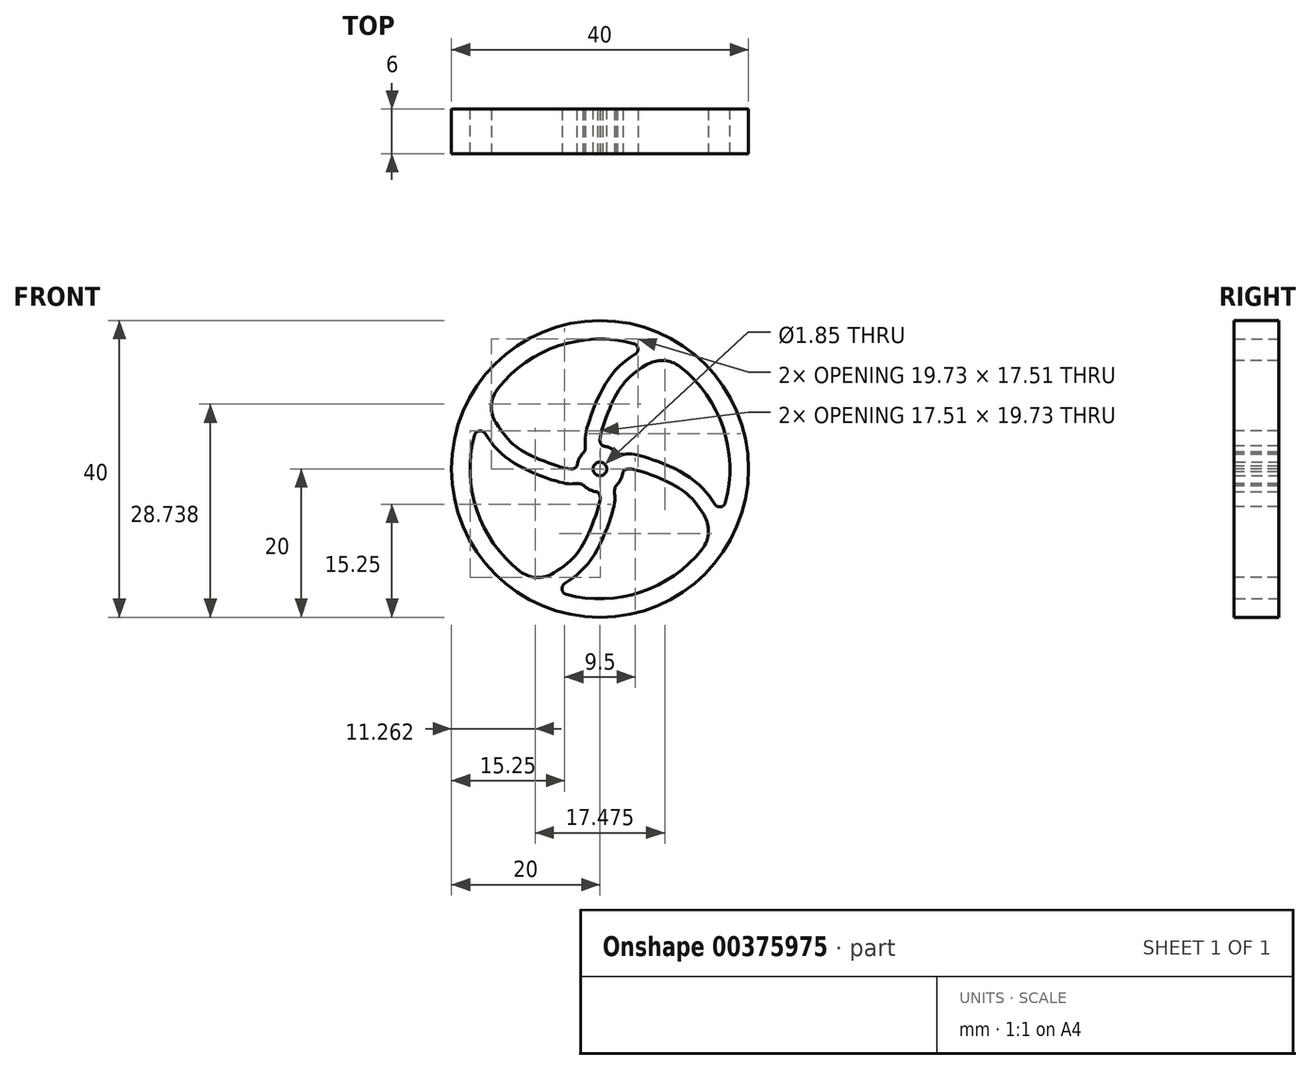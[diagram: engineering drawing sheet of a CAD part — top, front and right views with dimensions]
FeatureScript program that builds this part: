
annotation { "Feature Type Name" : "Feature", "Feature Type Description" : "" }
export const myFeature = defineFeature(function(context is Context, id is Id, definition is map)
    precondition{}
    {
        {
            var Q0;
            Q0=qCreatedBy(makeId("Front.planeOp"),FACE);
            var sketch = newSketch(context, id + "F0", { "sketchPlane" : qUnion([Q0])});
            skCircle(sketch, "E0", {"center": v(0, 0) * mm, "radius": 20 * mm});
            skCircle(sketch, "E1", {"center": v(0, 0) * mm, "radius": 0.93 * mm});
            skCircle(sketch, "E2", {"center": v(0, 0) * mm, "radius": 3.12 * mm});
            skCircle(sketch, "E3", {"center": v(0, 0) * mm, "radius": 17.5 * mm});
            skSolve(sketch);
        }
        {
            var Q0;
            Q0=qSketchRegion(id+"F0",true);
            var Q1;
            Q1=makeQuery(id+"F0.imprint","IMPRINT",FACE,{"disambiguationData":[TD([[makeQuery(id+"F0.imprint","IMPRINT",EDGE,{"derivedFrom":sQuery(id+"F0.wireOp",EDGE,"E1")}),-1.0]])]});
            extrude(context, id + "F1", {"entities" : qUnion([Q0, Q1]), "depth" : 6 * mm});
        }
        {
            var Q0;
            Q0=qCreatedBy(makeId("Right.planeOp"),FACE);
            var sketch = newSketch(context, id + "F2", { "sketchPlane" : qUnion([Q0])});
            skLineSegment(sketch, "E4", {"start": v(0, 17.54) * mm, "end": v(2.14, 1.57) * mm});
            skLineSegment(sketch, "E5", {"start": v(2.14, 1.57) * mm, "end": v(5.63, 1.57) * mm});
            skLineSegment(sketch, "E6", {"start": v(5.63, 1.57) * mm, "end": v(5.63, 19) * mm});
            skLineSegment(sketch, "E7", {"start": v(5.63, 19) * mm, "end": v(0, 19) * mm});
            skLineSegment(sketch, "E8", {"start": v(0, 19) * mm, "end": v(0, 17.54) * mm});
            skLineSegment(sketch, "E9", {"start": v(-16.5, 0) * mm, "end": v(18.02, 0) * mm});
            skLineSegment(sketch, "E10", {"start": v(18.02, 0) * mm, "end": v(18.02, 0.48) * mm});
            skSolve(sketch);
        }
        {
            var Q0;
            Q0=qSketchRegion(id+"F2",true);
            var Q1;
            Q1=sQuery(id+"F2.wireOp",EDGE,"E9");
            revolve(context, id + "F3", {"operationType" : NewBodyOperationType.REMOVE, "entities" : qUnion([Q0]), "axis" : qUnion([Q1]), "revolveType" : RevolveType.FULL});
        }
        {
            var Q0;
            Q0=makeQuery(id+"F1.opExtrude","CAP_FACE",FACE,{"disambiguationData":[OSD([sQuery(id+"F0.wireOp",EDGE,"E0"),sQuery(id+"F0.wireOp",EDGE,"E3")])],"isStart":false});
            var sketch = newSketch(context, id + "F4", { "sketchPlane" : qUnion([Q0])});
            skFitSpline(sketch, "E11", {"points": [v(-1.82, 2.4) * mm, v(-2, 3.75) * mm, v(-1.7, 5.68) * mm, v(1.39, 12.44) * mm, v(6.22, 16.36) * mm], "startDerivative": vector(-1.76, 9.05) * mm, "endDerivative": vector(16.16, 9.6) * mm});
            skFitSpline(sketch, "E12", {"points": [v(0.11, 2.97) * mm, v(0, 4.12) * mm, v(1.76, 9.17) * mm, v(4.06, 12.43) * mm, v(8.43, 15.33) * mm], "startDerivative": vector(-1.88, 6.55) * mm, "endDerivative": vector(16.22, 9.41) * mm});
            skArc(sketch, "E13.filletArc", {"start": v(10.8, 13.76) * mm, "mid": v(8.54, 14.61) * mm, "end": v(6.2, 14) * mm});
            skArc(sketch, "E14.filletArc", {"start": v(4.75, 15.46) * mm, "mid": v(5.11, 16.26) * mm, "end": v(4.53, 16.9) * mm});
            skArc(sketch, "E15.filletArc", {"start": v(-2.38, 1.85) * mm, "mid": v(-2.03, 2.54) * mm, "end": v(-1.97, 3.32) * mm});
            skPoint(sketch, "E16.visualSharp", {"position": v(0.1, 3) * mm});
            skArc(sketch, "E16.filletArc", {"start": v(-0.02, 3.96) * mm, "mid": v(0.17, 3.3) * mm, "end": v(0.74, 2.92) * mm});
            skArc(sketch, "E17", {"start": v(10.8, 13.76) * mm, "mid": v(7.83, 15.65) * mm, "end": v(4.53, 16.9) * mm});
            skArc(sketch, "E18", {"start": v(0.74, 2.92) * mm, "mid": v(-0.98, 2.85) * mm, "end": v(-2.38, 1.85) * mm});
            skSolve(sketch);
        }
        {
            var Q0;
            Q0 = qSketchRegion(id + "F4", true);
            extrude(context, id + "F5", {"entities" : qUnion([Q0]), "oppositeDirection" : true, "depth" : 6 * mm});
        }
        {
            var Q0;
            Q0=makeQuery(id+"F5.opExtrude","SWEPT_BODY",BODY,{"disambiguationData":[OSD([sQuery(id+"F4.wireOp",EDGE,"E11"),sQuery(id+"F4.wireOp",EDGE,"E12"),sQuery(id+"F4.wireOp",EDGE,"E13.filletArc"),sQuery(id+"F4.wireOp",EDGE,"E14.filletArc"),sQuery(id+"F4.wireOp",EDGE,"E15.filletArc"),sQuery(id+"F4.wireOp",EDGE,"E16.filletArc"),sQuery(id+"F4.wireOp",EDGE,"E17"),sQuery(id+"F4.wireOp",EDGE,"E18")])]});
            var Q1;
            Q1=makeQuery(id+"F1.opExtrude","CAP_EDGE",EDGE,{"disambiguationData":[OSD([sQuery(id+"F0.wireOp",EDGE,"E0")])],"isStart":false});
            circularPattern(context, id + "F6", {"operationType" : NewBodyOperationType.ADD, "entities" : qUnion([Q0]), "axis" : qUnion([Q1]), "angle" : 360 * degree, "instanceCount" : 4, "equalSpace" : true});
        }
    });
